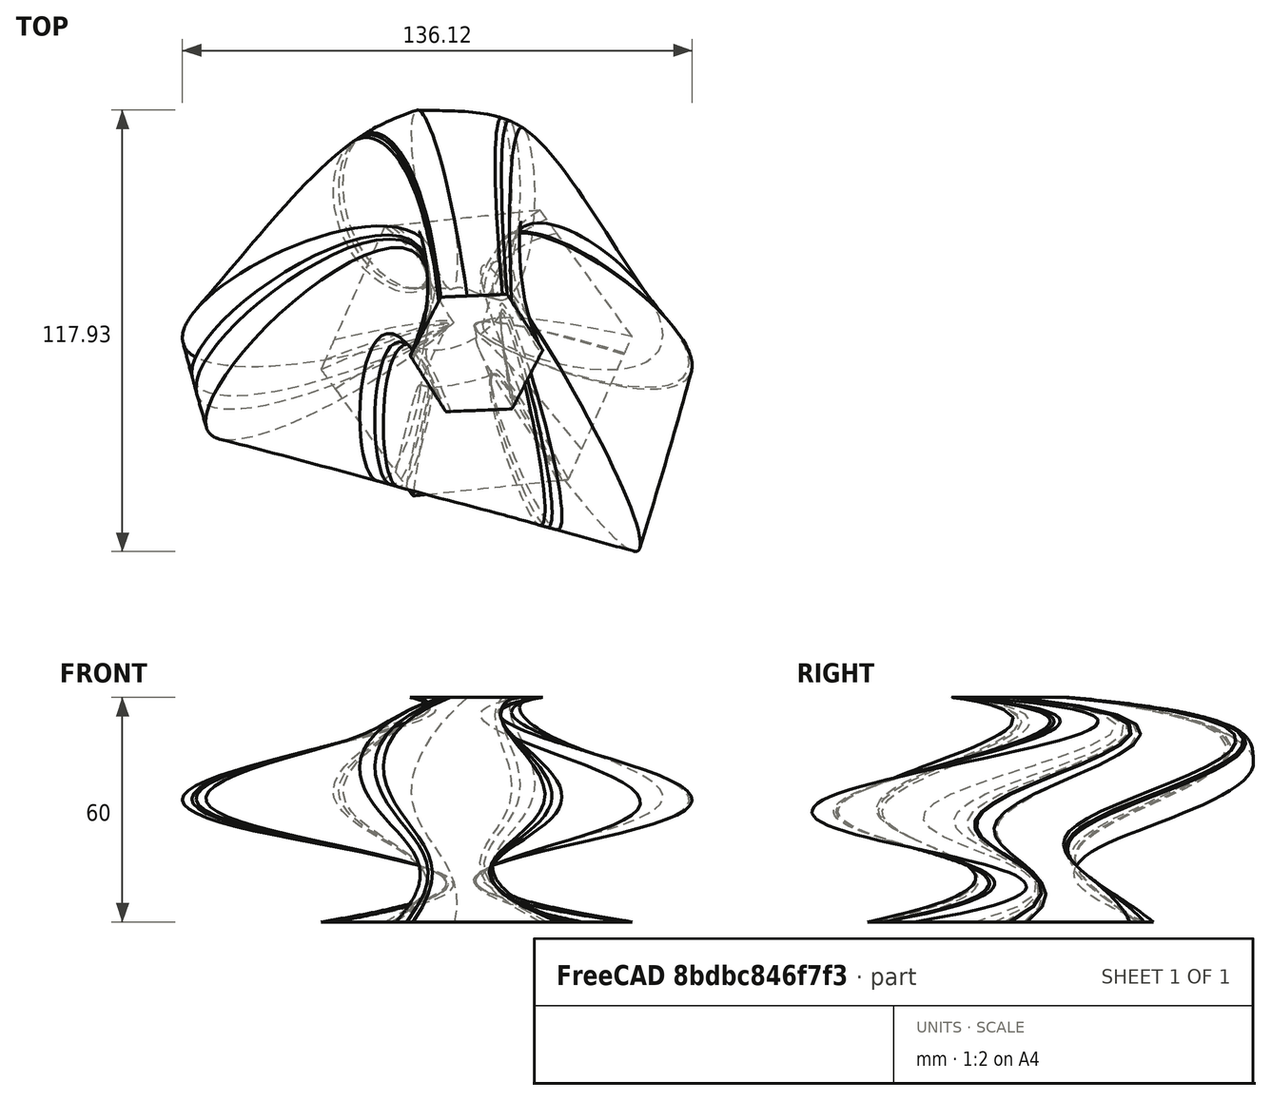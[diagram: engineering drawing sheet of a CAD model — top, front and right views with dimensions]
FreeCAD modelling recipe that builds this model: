
FCSTD DOCUMENT  (FreeCAD 0.21R33771 (Git))
Label: loft
License: All rights reserved
LicenseURL: https://en.wikipedia.org/wiki/All_rights_reserved
objects: Sketcher::SketchObject×5, PartDesign::Body×1, Part::Loft×1
note: 7 computed .brp shape members not serialized (recipe doc carries the construction recipe); baked Part::Feature solids carry a one-line shape summary decoded from their .brp

FEATURE [Sketcher::SketchObject] Sketch
  FullyConstrained = false
  MapMode = 5
  Support = -> [XY_Plane]
  sketch-geometry (7):
    g0: LineSegment StartX=24.5731 StartY=-33.7722 StartZ=0 EndX=41.5341 EndY=4.39488 EndZ=0
    g1: LineSegment StartX=41.5341 StartY=4.39488 StartZ=0 EndX=16.961 EndY=38.1671 EndZ=0
    g2: LineSegment StartX=16.961 StartY=38.1671 StartZ=0 EndX=-24.5731 EndY=33.7722 EndZ=0
    g3: LineSegment StartX=-24.5731 StartY=33.7722 StartZ=0 EndX=-41.5341 EndY=-4.39488 EndZ=0
    g4: LineSegment StartX=-41.5341 StartY=-4.39488 StartZ=0 EndX=-16.961 EndY=-38.1671 EndZ=0
    g5: LineSegment StartX=-16.961 StartY=-38.1671 StartZ=0 EndX=24.5731 EndY=-33.7722 EndZ=0
    g6: Circle CenterX=0 CenterY=0 CenterZ=0 NormalX=0 NormalY=0 NormalZ=1 AngleXU=0 Radius=41.766
  constraints (14):
    c: Coincident(g0,g1)
    c: Coincident(g1,g2)
    c: Coincident(g2,g3)
    c: Coincident(g3,g4)
    c: Coincident(g4,g5)
    c: Coincident(g5,g0)
    c: Equal(g0, g1-g5) x5
    c: PointOnObject(g0,g6)
    c: PointOnObject(g1,g6)
    c: PointOnObject(g2,g6)
    c: PointOnObject(g3,g6)
    c: PointOnObject(g4,g6)
    c: PointOnObject(g5,g6)
    c: Coincident(g6,g-1)
FEATURE [Sketcher::SketchObject] Sketch001
  AttachmentOffset = pos=(0,0,15) rot=(0,0,1;0rad)
  FullyConstrained = false
  MapMode = 5
  Placement = pos=(0,0,15) rot=(0,0,1;0rad)
  Support = -> [XY_Plane]
  sketch-geometry (4):
    g0: LineSegment StartX=-15.3276 StartY=17.5698 StartZ=0 EndX=4.28208 EndY=17.5698 EndZ=0
    g1: LineSegment StartX=4.28208 StartY=17.5698 StartZ=0 EndX=4.28208 EndY=-11.4724 EndZ=0
    g2: LineSegment StartX=4.28208 StartY=-11.4724 StartZ=0 EndX=-15.3276 EndY=-11.4724 EndZ=0
    g3: LineSegment StartX=-15.3276 StartY=-11.4724 StartZ=0 EndX=-15.3276 EndY=17.5698 EndZ=0
  constraints (8):
    c: Coincident(g0,g1)
    c: Coincident(g1,g2)
    c: Coincident(g2,g3)
    c: Coincident(g3,g0)
    c: Horizontal(g0)
    c: Horizontal(g2)
    c: Vertical(g1)
    c: Vertical(g3)
FEATURE [Sketcher::SketchObject] Sketch002
  AttachmentOffset = pos=(0,0,30) rot=(0,0,1;0rad)
  FullyConstrained = false
  MapMode = 5
  Placement = pos=(0,0,30) rot=(0,0,1;0rad)
  Support = -> [XY_Plane]
  sketch-geometry (5):
    g0: LineSegment StartX=-16.5687 StartY=48.3495 StartZ=0 EndX=-76.6389 EndY=0 EndZ=0
    g1: LineSegment StartX=-76.6389 StartY=0 StartZ=0 EndX=-70.185 EndY=-22.3943 EndZ=0
    g2: LineSegment StartX=-70.185 StartY=-22.3943 StartZ=0 EndX=43.005 EndY=-52.9258 EndZ=0
    g3: LineSegment StartX=43.005 StartY=-52.9258 StartZ=0 EndX=55.9126 EndY=-7.25263 EndZ=0
    g4: LineSegment StartX=55.9126 StartY=-7.25263 StartZ=0 EndX=-16.5687 EndY=48.3495 EndZ=0
  constraints (6):
    c: PointOnObject(g0,g-1)
    c: Coincident(g0,g1)
    c: Coincident(g1,g2)
    c: Coincident(g2,g3)
    c: Coincident(g3,g4)
    c: Coincident(g4,g0)
FEATURE [Sketcher::SketchObject] Sketch003
  AttachmentOffset = pos=(0,0,45) rot=(0,0,1;0rad)
  FullyConstrained = false
  MapMode = 5
  Placement = pos=(0,0,45) rot=(0,0,1;0rad)
  Support = -> [XY_Plane]
  sketch-geometry (1):
    g0: Circle CenterX=-8.37734 CenterY=25.2647 CenterZ=0 NormalX=0 NormalY=0 NormalZ=1 AngleXU=0 Radius=39.4707
FEATURE [Sketcher::SketchObject] Sketch004
  AttachmentOffset = pos=(0,0,60) rot=(0,0,1;0rad)
  FullyConstrained = false
  MapMode = 5
  Placement = pos=(0,0,60) rot=(0,0,1;0rad)
  Support = -> [XY_Plane]
  sketch-geometry (7):
    g0: LineSegment StartX=9.49477 StartY=-14.9476 StartZ=0 EndX=17.6924 EndY=0.748934 EndZ=0
    g1: LineSegment StartX=17.6924 StartY=0.748934 StartZ=0 EndX=8.19758 EndY=15.6965 EndZ=0
    g2: LineSegment StartX=8.19758 StartY=15.6965 StartZ=0 EndX=-9.49477 EndY=14.9476 EndZ=0
    g3: LineSegment StartX=-9.49477 StartY=14.9476 StartZ=0 EndX=-17.6924 EndY=-0.748934 EndZ=0
    g4: LineSegment StartX=-17.6924 StartY=-0.748934 StartZ=0 EndX=-8.19758 EndY=-15.6965 EndZ=0
    g5: LineSegment StartX=-8.19758 StartY=-15.6965 StartZ=0 EndX=9.49477 EndY=-14.9476 EndZ=0
    g6: Circle CenterX=0 CenterY=0 CenterZ=0 NormalX=0 NormalY=0 NormalZ=1 AngleXU=0 Radius=17.7082
  constraints (14):
    c: Coincident(g0,g1)
    c: Coincident(g1,g2)
    c: Coincident(g2,g3)
    c: Coincident(g3,g4)
    c: Coincident(g4,g5)
    c: Coincident(g5,g0)
    c: Equal(g0, g1-g5) x5
    c: PointOnObject(g0,g6)
    c: PointOnObject(g1,g6)
    c: PointOnObject(g2,g6)
    c: PointOnObject(g3,g6)
    c: PointOnObject(g4,g6)
    c: PointOnObject(g5,g6)
    c: Coincident(g6,g-1)
FEATURE [PartDesign::Body] Body
  Group = -> [Sketch,Sketch001,Sketch002,Sketch003,Sketch004]
  Origin = -> Origin
FEATURE [Part::Loft] Loft
  Closed = false
  MaxDegree = 5
  Ruled = false
  Sections = -> [Sketch,Sketch001,Sketch002,Sketch003,Sketch004]
  Solid = true
